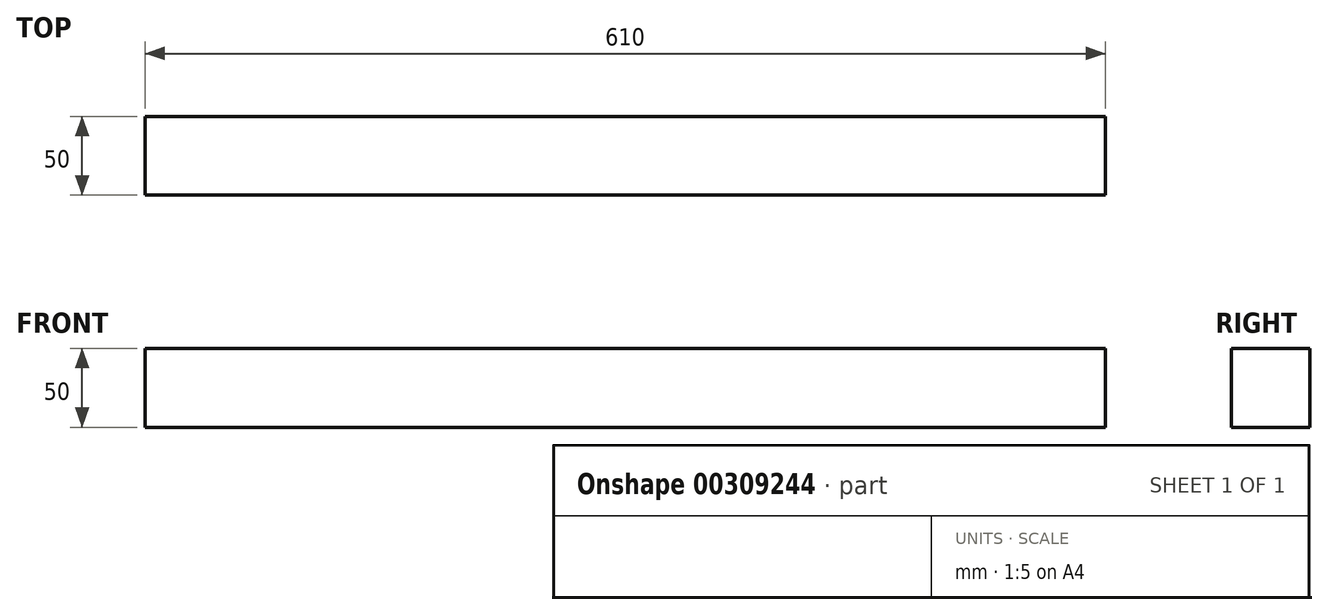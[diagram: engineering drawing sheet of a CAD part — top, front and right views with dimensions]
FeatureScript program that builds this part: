
annotation { "Feature Type Name" : "Feature", "Feature Type Description" : "" }
export const myFeature = defineFeature(function(context is Context, id is Id, definition is map)
    precondition{}
    {
        {
            var Q0;
            Q0=qCreatedBy(makeId("Right.planeOp"),FACE);
            var sketch = newSketch(context, id + "F0", { "sketchPlane" : qUnion([Q0])});
            skLineSegment(sketch, "E0.bottom", {"start": v(0, 0) * mm, "end": v(50, 0) * mm});
            skLineSegment(sketch, "E0.top", {"start": v(0, 50) * mm, "end": v(50, 50) * mm});
            skLineSegment(sketch, "E0.left", {"start": v(0, 0) * mm, "end": v(0, 50) * mm});
            skLineSegment(sketch, "E0.right", {"start": v(50, 0) * mm, "end": v(50, 50) * mm});
            skSolve(sketch);
        }
        {
            var Q0;
            Q0=makeQuery(id+"F0.imprint","IMPRINT",FACE,{"disambiguationData":[TD([[makeQuery(id+"F0.imprint","IMPRINT",EDGE,{"derivedFrom":sQuery(id+"F0.wireOp",EDGE,"E0.bottom")}),1.0]])]});
            extrude(context, id + "F1", {"entities" : qUnion([Q0]), "oppositeDirection" : true, "depth" : 610 * mm});
        }
    });
